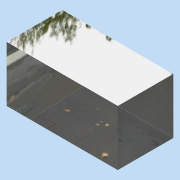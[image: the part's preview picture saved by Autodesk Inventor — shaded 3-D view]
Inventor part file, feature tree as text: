
AUTODESK INVENTOR PART (.ipt)
format: ipt  version: 2015 (Build 190159000, 159)  size: 91,136 bytes
history: native  units: in
note: dims shown in document units (in); Inventor stores cm internally (conversion verified against a paired STEP export)
features: extrude x1, sketch x1
ambient origin geometry x8: Origin, YZ Plane, XZ Plane, XY Plane, X Axis, Y Axis, Z Axis, Center Point
bodies: Solid1 (feature_tree)
feature tree (2):
  extrude  "Extrusion1"  Depth=0.25in
  sketch  "Sketch1"  dims[d0=0.5in d1=0.25in d2=0.25in d3=0.0in]
